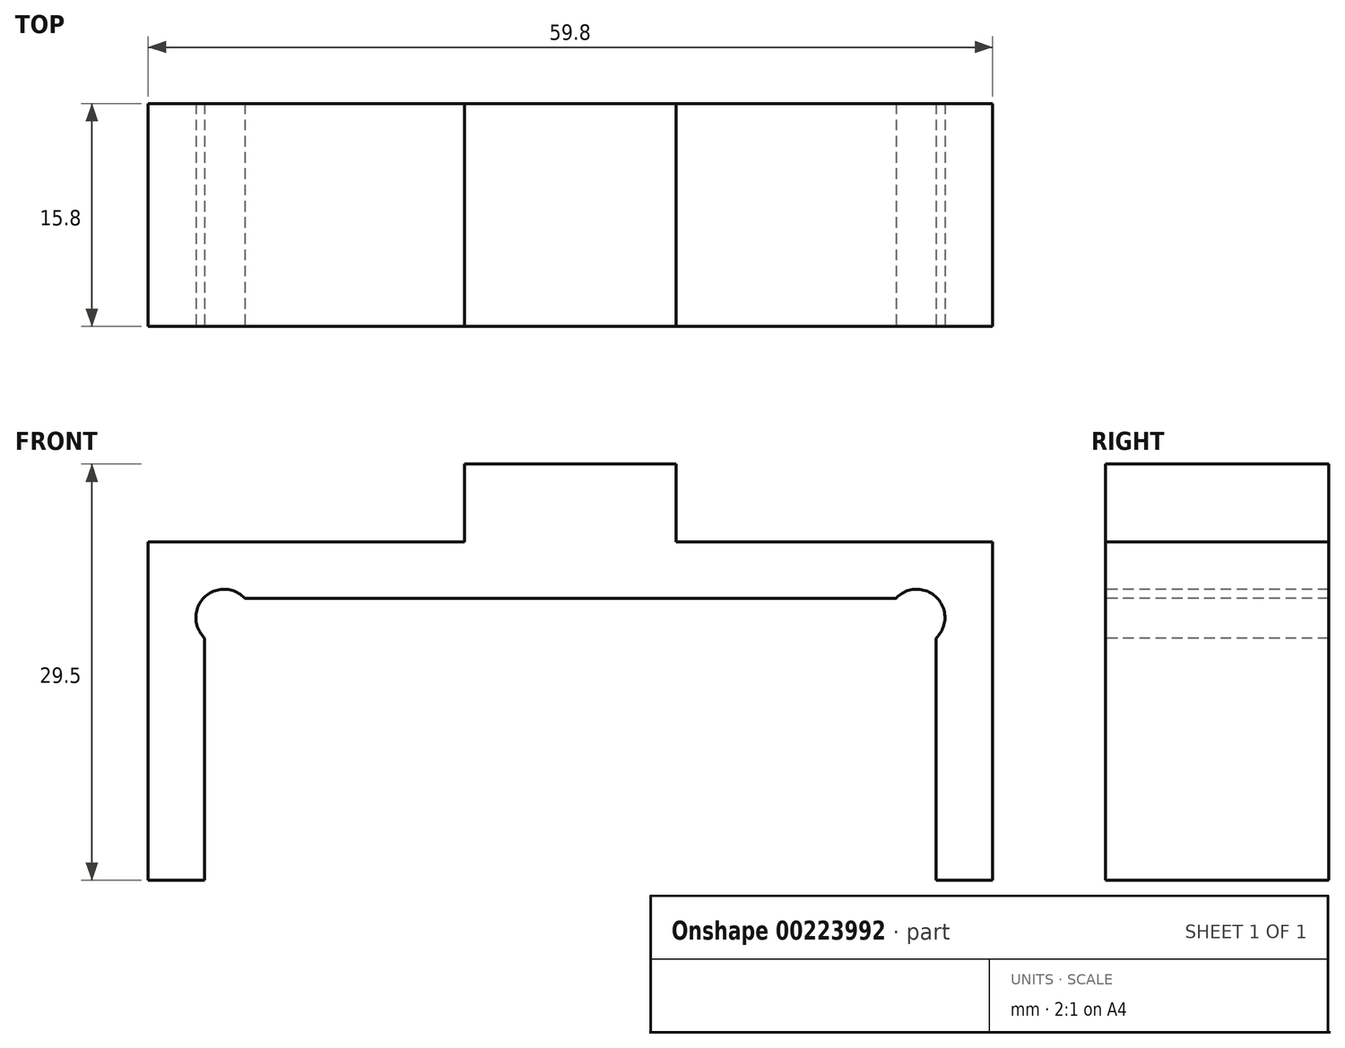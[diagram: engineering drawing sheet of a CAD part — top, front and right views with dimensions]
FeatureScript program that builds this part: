
annotation { "Feature Type Name" : "Feature", "Feature Type Description" : "" }
export const myFeature = defineFeature(function(context is Context, id is Id, definition is map)
    precondition{}
    {
        {
            var Q0;
            Q0=qCreatedBy(makeId("Front.planeOp"),FACE);
            var sketch = newSketch(context, id + "F0", { "sketchPlane" : qUnion([Q0])});
            skLineSegment(sketch, "E0", {"start": v(-25.9, 0) * mm, "end": v(25.9, 0) * mm});
            skLineSegment(sketch, "E1", {"start": v(25.9, 0) * mm, "end": v(25.9, -20) * mm});
            skLineSegment(sketch, "E2", {"start": v(25.9, -20) * mm, "end": v(29.9, -20) * mm});
            skLineSegment(sketch, "E3", {"start": v(29.9, -20) * mm, "end": v(29.9, 4) * mm});
            skLineSegment(sketch, "E4", {"start": v(29.9, 4) * mm, "end": v(-29.9, 4) * mm});
            skLineSegment(sketch, "E5", {"start": v(-29.9, 4) * mm, "end": v(-29.9, -20) * mm});
            skLineSegment(sketch, "E6", {"start": v(-25.9, 0) * mm, "end": v(-25.9, -20) * mm});
            skLineSegment(sketch, "E7", {"start": v(-29.9, -20) * mm, "end": v(-25.9, -20) * mm});
            skLineSegment(sketch, "E8", {"start": v(0, 4) * mm, "end": v(0, 0) * mm, "construction": true});
            skSolve(sketch);
        }
        {
            var Q0;
            Q0=qSketchRegion(id+"F0",true);
            extrude(context, id + "F1", {"entities" : qUnion([Q0]), "depth" : 15.8 * mm});
        }
        {
            var Q0;
            Q0=makeQuery(id+"F1.opExtrude","SWEPT_FACE",FACE,{"disambiguationData":[OSD([sQuery(id+"F0.wireOp",EDGE,"E4")])]});
            var sketch = newSketch(context, id + "F2", { "sketchPlane" : qUnion([Q0])});
            skLineSegment(sketch, "E9", {"start": v(0, 0) * mm, "end": v(0, -15.8) * mm, "construction": true});
            skLineSegment(sketch, "E10.bottom", {"start": v(7.5, 0) * mm, "end": v(-7.5, 0) * mm});
            skLineSegment(sketch, "E10.top", {"start": v(7.5, -15.8) * mm, "end": v(-7.5, -15.8) * mm});
            skLineSegment(sketch, "E10.left", {"start": v(7.5, 0) * mm, "end": v(7.5, -15.8) * mm});
            skLineSegment(sketch, "E10.right", {"start": v(-7.5, 0) * mm, "end": v(-7.5, -15.8) * mm});
            skPoint(sketch, "E10.middle", {"position": v(0, -7.9) * mm});
            skSolve(sketch);
        }
        {
            var Q0;
            Q0=qSketchRegion(id+"F2",true);
            extrude(context, id + "F3", {"entities" : qUnion([Q0]), "operationType" : NewBodyOperationType.ADD, "depth" : 5.5 * mm});
        }
        {
            var Q0;
            Q0=makeQuery(id+"F3.boolean.opBoolean","MERGE",FACE,{"derivedFrom":[makeQuery(id+"FmveGxebxOgO2IK_1.boolean.opBoolean","MERGE",FACE,{"derivedFrom":[makeQuery(id+"F1.opExtrude","CAP_FACE",FACE,{"disambiguationData":[OSD([sQuery(id+"F0.wireOp",EDGE,"E0"),sQuery(id+"F0.wireOp",EDGE,"E1"),sQuery(id+"F0.wireOp",EDGE,"E2"),sQuery(id+"F0.wireOp",EDGE,"E3"),sQuery(id+"F0.wireOp",EDGE,"E4"),sQuery(id+"F0.wireOp",EDGE,"E5"),sQuery(id+"F0.wireOp",EDGE,"E6"),sQuery(id+"F0.wireOp",EDGE,"E7")])],"isStart":false}),makeQuery(id+"FmveGxebxOgO2IK_1.opExtrude","CAP_FACE",FACE,{"disambiguationData":[OSD([sQuery(id+"FWKaNPGXON1Dya7_1.wireOp",EDGE,"jeChqFw1-5VWL-QMwC-h4n7-nWrUDRxe8OVh.bottom"),sQuery(id+"FWKaNPGXON1Dya7_1.wireOp",EDGE,"jeChqFw1-5VWL-QMwC-h4n7-nWrUDRxe8OVh.top"),sQuery(id+"FWKaNPGXON1Dya7_1.wireOp",EDGE,"jeChqFw1-5VWL-QMwC-h4n7-nWrUDRxe8OVh.left"),sQuery(id+"FWKaNPGXON1Dya7_1.wireOp",EDGE,"jeChqFw1-5VWL-QMwC-h4n7-nWrUDRxe8OVh.right")])],"isStart":true})]}),makeQuery(id+"F3.opExtrude","SWEPT_FACE",FACE,{"disambiguationData":[OSD([sQuery(id+"F2.wireOp",EDGE,"E10.top")])]})]});
            var sketch = newSketch(context, id + "F4", { "sketchPlane" : qUnion([Q0])});
            skLineSegment(sketch, "E11", {"start": v(-25.9, 0) * mm, "end": v(-7.12, -18.78) * mm, "construction": true});
            skCircle(sketch, "E12", {"center": v(-24.53, -1.37) * mm, "radius": 2 * mm});
            skCircle(sketch, "E13.MirrorC", {"center": v(24.53, -1.37) * mm, "radius": 2 * mm});
            skSolve(sketch);
        }
        {
            var Q0;
            Q0=qSketchRegion(id+"F4",true);
            extrude(context, id + "F5", {"entities" : qUnion([Q0]), "operationType" : NewBodyOperationType.REMOVE, "endBound" : BoundingType.THROUGH_ALL, "oppositeDirection" : true, "depth" : 25 * mm});
        }
    });
